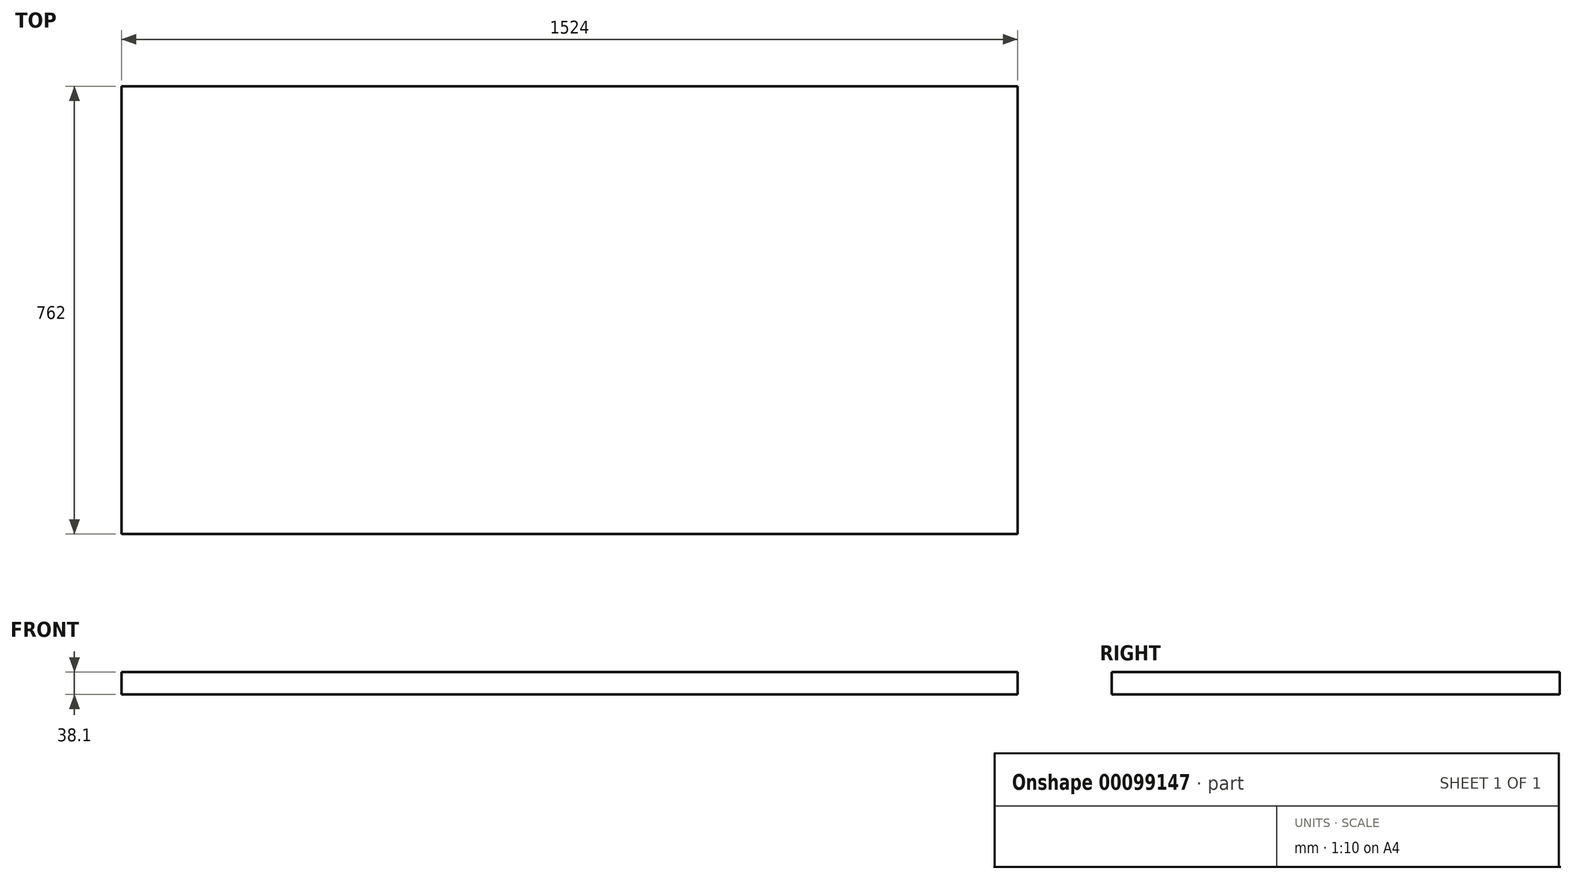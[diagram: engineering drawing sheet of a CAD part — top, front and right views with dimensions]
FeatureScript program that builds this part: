
annotation { "Feature Type Name" : "Feature", "Feature Type Description" : "" }
export const myFeature = defineFeature(function(context is Context, id is Id, definition is map)
    precondition{}
    {
        {
            var Q0;
            Q0=qCreatedBy(makeId("Top.planeOp"),FACE);
            var sketch = newSketch(context, id + "F0", { "sketchPlane" : qUnion([Q0])});
            skPoint(sketch, "E0", {"position": v(0, 381) * mm});
            skPoint(sketch, "E1", {"position": v(0, -381) * mm});
            skPoint(sketch, "E2", {"position": v(762, 0) * mm});
            skPoint(sketch, "E3", {"position": v(-762, 0) * mm});
            skPoint(sketch, "E4", {"position": v(-762, 381) * mm});
            skPoint(sketch, "E5", {"position": v(762, -381) * mm});
            skLineSegment(sketch, "E6.bottom", {"start": v(-762, 381) * mm, "end": v(762, 381) * mm});
            skLineSegment(sketch, "E6.top", {"start": v(-762, -381) * mm, "end": v(762, -381) * mm});
            skLineSegment(sketch, "E6.left", {"start": v(-762, 381) * mm, "end": v(-762, -381) * mm});
            skLineSegment(sketch, "E6.right", {"start": v(762, 381) * mm, "end": v(762, -381) * mm});
            skSolve(sketch);
        }
        {
            var Q0;
            Q0=makeQuery(id+"F0.imprint","IMPRINT",FACE,{"disambiguationData":[TD([[makeQuery(id+"F0.imprint","IMPRINT",EDGE,{"derivedFrom":sQuery(id+"F0.wireOp",EDGE,"E6.bottom")}),-1.0]])]});
            extrude(context, id + "F1", {"entities" : qUnion([Q0]), "depth" : 38.1 * mm});
        }
    });
